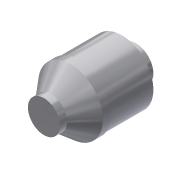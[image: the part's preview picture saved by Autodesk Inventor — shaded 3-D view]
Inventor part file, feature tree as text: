
AUTODESK INVENTOR PART (.ipt)
format: ipt  version: 2019.4 (Build 234330000, 330)  size: 108,032 bytes
history: native  units: mm
features: revolve x1, sketch x1
ambient origin geometry x8: Origin, YZ Plane, XZ Plane, XY Plane, X Axis, Y Axis, Z Axis, Center Point
bodies: Solid1 (feature_tree)
feature tree (2):
  revolve  "Revolution1"  [1 undecoded]
  sketch  "Sketch1"  dims[d0=7.78mm d1=6.36mm d2=41.4mm d3=7.21mm d4=14.5mm d5=90.0deg]
note: 1 required parameter value undecoded (feature->parameter linkage not recoverable at this tier; creation-order binding heuristic only, values carry confidence <= 0.55)
